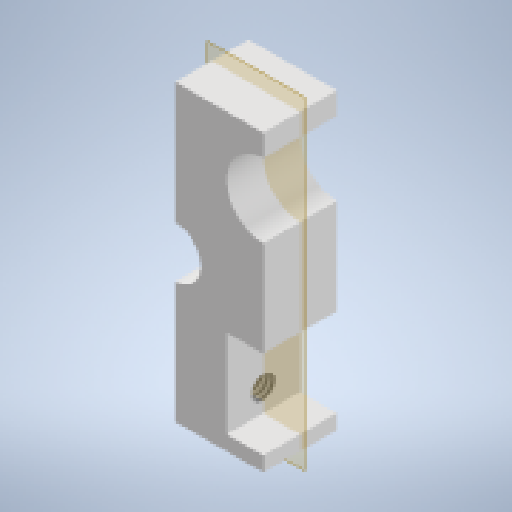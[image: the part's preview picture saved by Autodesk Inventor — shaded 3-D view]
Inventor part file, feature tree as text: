
AUTODESK INVENTOR PART (.ipt)
format: ipt  version: 2023 (Build 270158000, 158)  size: 236,032 bytes
history: native  units: mm
features: extrude x7, sketch x7, thread x2, plane x1
ambient origin geometry x8: Origin, YZ Plane, XZ Plane, XY Plane, X Axis, Y Axis, Z Axis, Center Point
bodies: Solid1 (feature_tree)
feature tree (17):
  extrude  "Extrusion1"  Depth=20.0mm
  plane  "Work Plane1"
  extrude  "Extrusion2"  Depth=2.0mm
  extrude  "Extrusion3"  Depth=4.0mm
  extrude  "Extrusion4"  Depth=5.0mm TaperAngle=0.0deg
  thread  "Thread1"  [1 undecoded]
  thread  "Thread2"  [1 undecoded]
  extrude  "Extrusion5"  Depth=8.0mm TaperAngle=0.0deg
  extrude  "Extrusion6"  Depth=1.6mm
  extrude  "Extrusion7"  Depth=10.0mm
  sketch  "Sketch1"  dims[d0=20.0mm d1=20.0mm]
  sketch  "Sketch2"  dims[d2=4.0mm d6=2.0mm]
  sketch  "Sketch3"  dims[d7=2.0mm d8=4.0mm]
  sketch  "Sketch4"  dims[d9=2.0mm d10=5.0mm d11=0.0mm d12=5.0mm d13=1.8mm d14=0.0mm]
  sketch  "Sketch5"  dims[d15=3.5mm d16=8.0mm d17=0.0mm]
  sketch  "Sketch6"  dims[d18=1.6mm d19=1.6mm]
  sketch  "Sketch7"  dims[d20=2.5mm d21=2.5mm d22=2.5mm d23=2.5mm d24=5.0mm d25=0.0mm d26=5.0mm d27=0.0mm d28=5.0mm d29=0.0mm d30=5.0mm d31=0.0mm d32=2.5mm d33=1.0mm d34=6.0mm d35=5.0mm d36=4.0mm d37=5.0mm d38=0.0mm d39=2.5mm d40=10.0mm d41=2.05mm d42=12.0mm d43=0.0mm]
note: 2 required parameter values undecoded (feature->parameter linkage not recoverable at this tier; creation-order binding heuristic only, values carry confidence <= 0.55)
